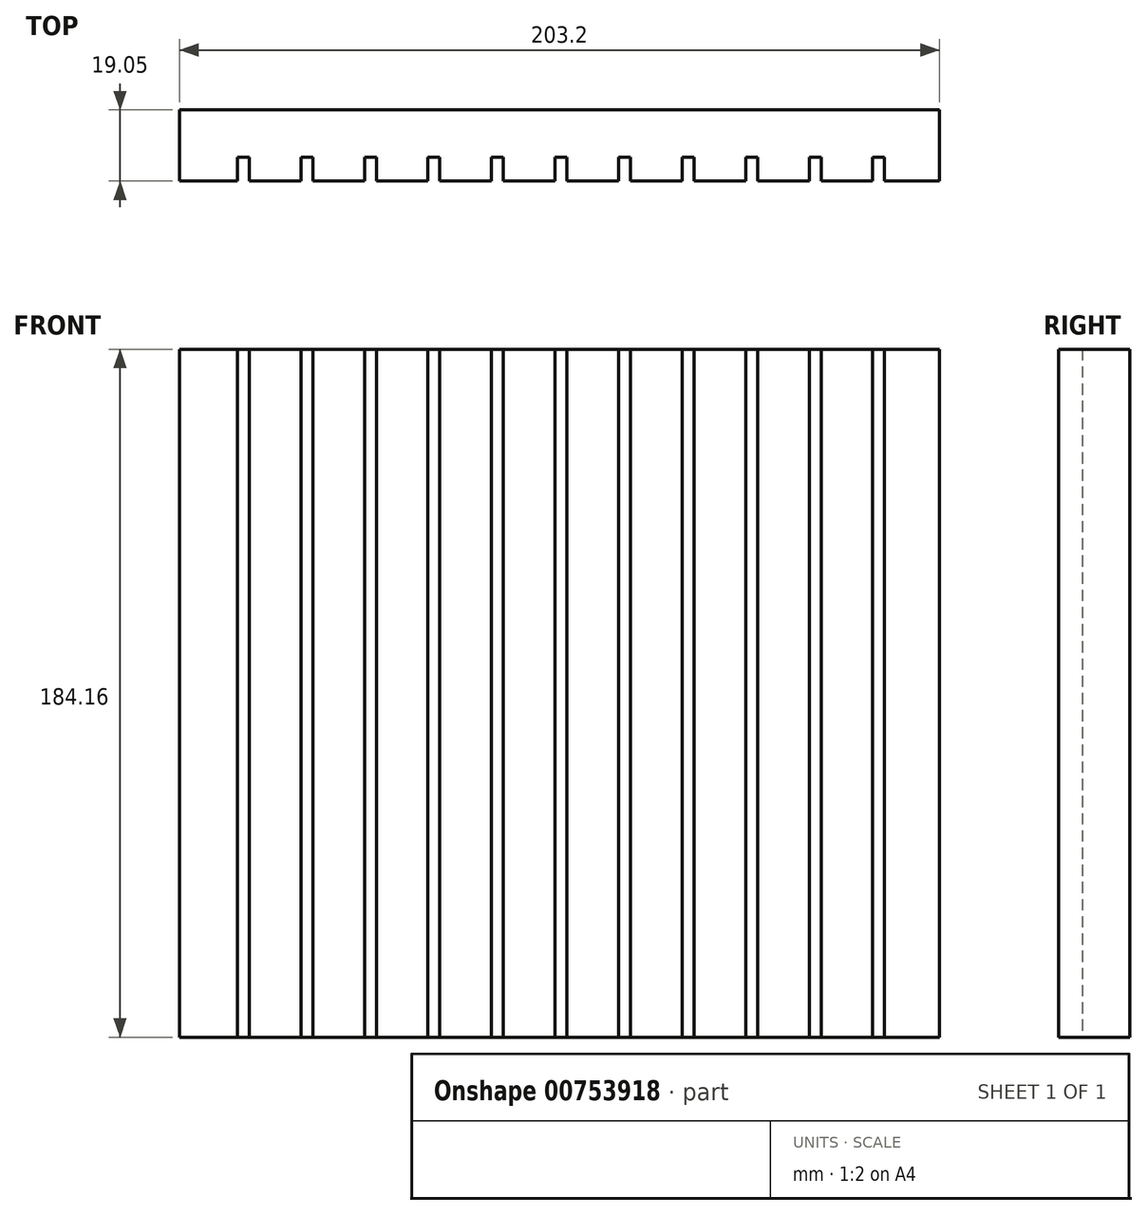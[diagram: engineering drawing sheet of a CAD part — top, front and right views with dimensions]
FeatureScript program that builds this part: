
annotation { "Feature Type Name" : "Feature", "Feature Type Description" : "" }
export const myFeature = defineFeature(function(context is Context, id is Id, definition is map)
    precondition{}
    {
        {
            var Q0;
            Q0=qCreatedBy(makeId("Front.planeOp"),FACE);
            var sketch = newSketch(context, id + "F0", { "sketchPlane" : qUnion([Q0])});
            skLineSegment(sketch, "E0.bottom", {"start": v(101.6, -92.07) * mm, "end": v(-101.6, -92.07) * mm});
            skLineSegment(sketch, "E0.top", {"start": v(101.6, 92.08) * mm, "end": v(-101.6, 92.07) * mm});
            skLineSegment(sketch, "E0.left", {"start": v(101.6, -92.07) * mm, "end": v(101.6, 92.08) * mm});
            skLineSegment(sketch, "E0.right", {"start": v(-101.6, -92.07) * mm, "end": v(-101.6, 92.08) * mm});
            skPoint(sketch, "E0.middle", {"position": v(0, 0) * mm});
            skSolve(sketch);
        }
        {
            var Q0;
            Q0=makeQuery(id+"F0.imprint","IMPRINT",FACE,{"disambiguationData":[TD([[makeQuery(id+"F0.imprint","IMPRINT",EDGE,{"derivedFrom":sQuery(id+"F0.wireOp",EDGE,"E0.bottom")}),-1.0]])]});
            extrude(context, id + "F1", {"entities" : qUnion([Q0]), "depth" : 19.05 * mm, "offsetDistance" : 25.4 * mm});
        }
        {
            var Q0;
            Q0=makeQuery(id+"F1.opExtrude","CAP_FACE",FACE,{"disambiguationData":[OSD([sQuery(id+"F0.wireOp",EDGE,"E0.bottom"),sQuery(id+"F0.wireOp",EDGE,"E0.top"),sQuery(id+"F0.wireOp",EDGE,"E0.left"),sQuery(id+"F0.wireOp",EDGE,"E0.right")])],"isStart":false});
            var sketch = newSketch(context, id + "F2", { "sketchPlane" : qUnion([Q0])});
            skLineSegment(sketch, "E1.0", {"start": v(-84.6, -92.07) * mm, "end": v(-84.6, 92.08) * mm, "construction": true});
            skLineSegment(sketch, "E2.bottom", {"start": v(-84.6, 92.08) * mm, "end": v(-83.01, 92.08) * mm, "construction": true});
            skLineSegment(sketch, "E2.top", {"start": v(-84.6, -92.07) * mm, "end": v(-83.01, -92.07) * mm, "construction": true});
            skLineSegment(sketch, "E2.left", {"start": v(-84.6, 92.08) * mm, "end": v(-84.6, -92.07) * mm, "construction": true});
            skLineSegment(sketch, "E3.bottom", {"start": v(-86.19, 92.08) * mm, "end": v(-83.01, 92.08) * mm});
            skLineSegment(sketch, "E3.top", {"start": v(-86.19, -92.07) * mm, "end": v(-83.01, -92.07) * mm});
            skLineSegment(sketch, "E3.left", {"start": v(-86.19, 92.08) * mm, "end": v(-86.19, -92.07) * mm});
            skLineSegment(sketch, "E3.right", {"start": v(-83.01, 92.08) * mm, "end": v(-83.01, -92.07) * mm});
            skLineSegment(sketch, "E4.1.0.0", {"start": v(-69.19, 92.08) * mm, "end": v(-69.19, -92.07) * mm});
            skLineSegment(sketch, "E4.1.0.1", {"start": v(-66.01, 92.08) * mm, "end": v(-66.01, -92.07) * mm});
            skLineSegment(sketch, "E4.2.0.0", {"start": v(-52.19, 92.08) * mm, "end": v(-52.19, -92.07) * mm});
            skLineSegment(sketch, "E4.2.0.1", {"start": v(-49.01, 92.08) * mm, "end": v(-49.01, -92.07) * mm});
            skLineSegment(sketch, "E4.3.0.0", {"start": v(-35.19, 92.08) * mm, "end": v(-35.19, -92.07) * mm});
            skLineSegment(sketch, "E4.3.0.1", {"start": v(-32.01, 92.08) * mm, "end": v(-32.01, -92.07) * mm});
            skLineSegment(sketch, "E4.4.0.0", {"start": v(-18.19, 92.08) * mm, "end": v(-18.19, -92.07) * mm});
            skLineSegment(sketch, "E4.4.0.1", {"start": v(-15.01, 92.08) * mm, "end": v(-15.01, -92.07) * mm});
            skLineSegment(sketch, "E4.5.0.0", {"start": v(-1.19, 92.08) * mm, "end": v(-1.19, -92.07) * mm});
            skLineSegment(sketch, "E4.5.0.1", {"start": v(1.99, 92.08) * mm, "end": v(1.99, -92.07) * mm});
            skLineSegment(sketch, "E4.6.0.0", {"start": v(15.81, 92.08) * mm, "end": v(15.81, -92.07) * mm});
            skLineSegment(sketch, "E4.6.0.1", {"start": v(18.99, 92.08) * mm, "end": v(18.99, -92.07) * mm});
            skLineSegment(sketch, "E4.7.0.0", {"start": v(32.81, 92.08) * mm, "end": v(32.81, -92.07) * mm});
            skLineSegment(sketch, "E4.7.0.1", {"start": v(35.99, 92.08) * mm, "end": v(35.99, -92.07) * mm});
            skLineSegment(sketch, "E4.8.0.0", {"start": v(49.81, 92.08) * mm, "end": v(49.81, -92.07) * mm});
            skLineSegment(sketch, "E4.8.0.1", {"start": v(52.99, 92.08) * mm, "end": v(52.99, -92.07) * mm});
            skLineSegment(sketch, "E4.9.0.0", {"start": v(66.81, 92.08) * mm, "end": v(66.81, -92.07) * mm});
            skLineSegment(sketch, "E4.9.0.1", {"start": v(69.99, 92.08) * mm, "end": v(69.99, -92.07) * mm});
            skLineSegment(sketch, "E4.direction1", {"start": v(-86.19, -92.07) * mm, "end": v(-69.19, -92.07) * mm, "construction": true});
            skLineSegment(sketch, "E5.0.10.0", {"start": v(83.81, 92.08) * mm, "end": v(83.81, -92.07) * mm});
            skLineSegment(sketch, "E5.3.10.0", {"start": v(86.99, 92.08) * mm, "end": v(86.99, -92.07) * mm});
            skSolve(sketch);
        }
        {
            var Q0;
            Q0=makeQuery(id+"F2.imprint","IMPRINT",FACE,{"disambiguationData":[TD([[makeQuery(id+"F2.imprint","IMPRINT",EDGE,{"derivedFrom":sQuery(id+"F2.wireOp",EDGE,"E3.bottom")}),1.0]])]});
            var Q1;
            {var subQ0=sQuery(id+"F2.wireOp",EDGE,"E4.1.0.0");Q1=makeQuery(id+"F2.imprint","IMPRINT",FACE,{"disambiguationData":[TD([[makeQuery(id+"F2.imprint","IMPRINT",EDGE,{"derivedFrom":subQ0}),1.0]])]});}
            var Q2;
            {var subQ0=sQuery(id+"F2.wireOp",EDGE,"E4.2.0.0");Q2=makeQuery(id+"F2.imprint","IMPRINT",FACE,{"disambiguationData":[TD([[makeQuery(id+"F2.imprint","IMPRINT",EDGE,{"derivedFrom":subQ0}),1.0]])]});}
            var Q3;
            {var subQ0=sQuery(id+"F2.wireOp",EDGE,"E4.3.0.0");Q3=makeQuery(id+"F2.imprint","IMPRINT",FACE,{"disambiguationData":[TD([[makeQuery(id+"F2.imprint","IMPRINT",EDGE,{"derivedFrom":subQ0}),1.0]])]});}
            var Q4;
            {var subQ0=sQuery(id+"F2.wireOp",EDGE,"E4.6.0.0");Q4=makeQuery(id+"F2.imprint","IMPRINT",FACE,{"disambiguationData":[TD([[makeQuery(id+"F2.imprint","IMPRINT",EDGE,{"derivedFrom":subQ0}),1.0]])]});}
            var Q5;
            {var subQ0=sQuery(id+"F2.wireOp",EDGE,"E4.7.0.0");Q5=makeQuery(id+"F2.imprint","IMPRINT",FACE,{"disambiguationData":[TD([[makeQuery(id+"F2.imprint","IMPRINT",EDGE,{"derivedFrom":subQ0}),1.0]])]});}
            var Q6;
            {var subQ0=sQuery(id+"F2.wireOp",EDGE,"E4.8.0.0");Q6=makeQuery(id+"F2.imprint","IMPRINT",FACE,{"disambiguationData":[TD([[makeQuery(id+"F2.imprint","IMPRINT",EDGE,{"derivedFrom":subQ0}),1.0]])]});}
            var Q7;
            {var subQ0=sQuery(id+"F2.wireOp",EDGE,"E4.9.0.0");Q7=makeQuery(id+"F2.imprint","IMPRINT",FACE,{"disambiguationData":[TD([[makeQuery(id+"F2.imprint","IMPRINT",EDGE,{"derivedFrom":subQ0}),1.0]])]});}
            var Q8;
            {var subQ0=sQuery(id+"F2.wireOp",EDGE,"E4.4.0.0");Q8=makeQuery(id+"F2.imprint","IMPRINT",FACE,{"disambiguationData":[TD([[makeQuery(id+"F2.imprint","IMPRINT",EDGE,{"derivedFrom":subQ0}),1.0]])]});}
            var Q9;
            {var subQ0=sQuery(id+"F2.wireOp",EDGE,"E4.5.0.0");Q9=makeQuery(id+"F2.imprint","IMPRINT",FACE,{"disambiguationData":[TD([[makeQuery(id+"F2.imprint","IMPRINT",EDGE,{"derivedFrom":subQ0}),1.0]])]});}
            var Q10;
            {var subQ0=sQuery(id+"F2.wireOp",EDGE,"E5.0.10.0");Q10=makeQuery(id+"F2.imprint","IMPRINT",FACE,{"disambiguationData":[TD([[makeQuery(id+"F2.imprint","IMPRINT",EDGE,{"derivedFrom":subQ0}),1.0]])]});}
            extrude(context, id + "F3", {"entities" : qUnion([Q0, Q1, Q2, Q3, Q4, Q5, Q6, Q7, Q8, Q9, Q10]), "operationType" : NewBodyOperationType.REMOVE, "oppositeDirection" : true, "depth" : 6.35 * mm, "offsetDistance" : 25.4 * mm});
        }
    });
